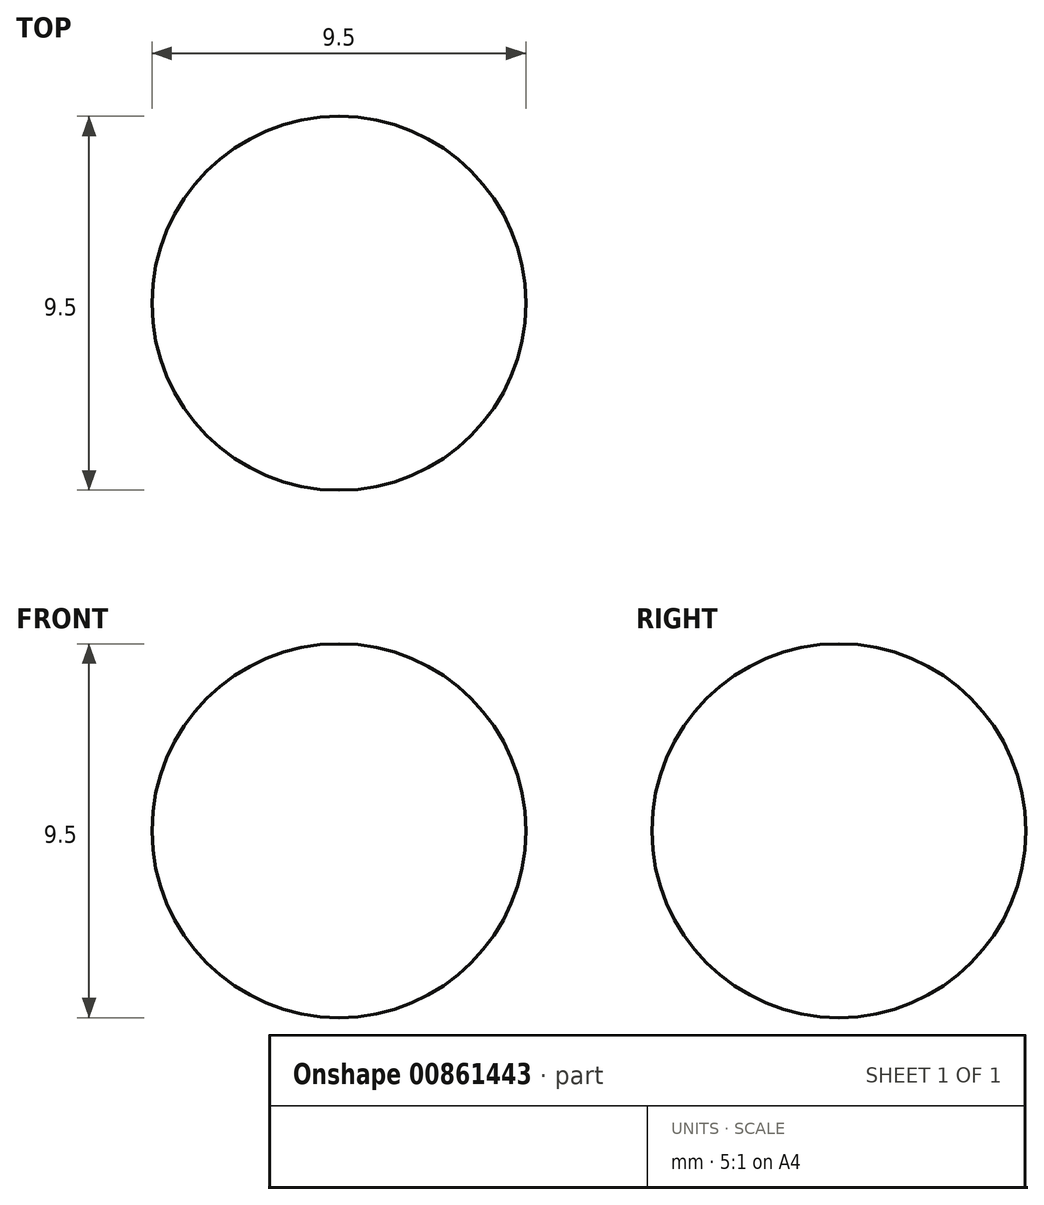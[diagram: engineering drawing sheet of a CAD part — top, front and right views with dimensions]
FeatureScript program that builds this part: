
annotation { "Feature Type Name" : "Feature", "Feature Type Description" : "" }
export const myFeature = defineFeature(function(context is Context, id is Id, definition is map)
    precondition{}
    {
        {
            var Q0;
            Q0=qCreatedBy(makeId("Front.planeOp"),FACE);
            var sketch = newSketch(context, id + "F0", { "sketchPlane" : qUnion([Q0])});
            skCircle(sketch, "E0", {"center": v(0, 0) * mm, "radius": 4.75 * mm});
            skLineSegment(sketch, "E1", {"start": v(0, 4.75) * mm, "end": v(0, -4.75) * mm});
            skSolve(sketch);
        }
        {
            var Q0;
            {var subQ0=sQuery(id+"F0.wireOp",EDGE,"E1");Q0=makeQuery(id+"F0.imprint","IMPRINT",FACE,{"disambiguationData":[TD([[makeQuery(id+"F0.imprint","IMPRINT",EDGE,{"derivedFrom":subQ0}),1.0]])]});}
            var Q1;
            Q1=sQuery(id+"F0.wireOp",EDGE,"E1");
            revolve(context, id + "F1", {"surfaceOperationType" : NewSurfaceOperationType.NEW, "entities" : qUnion([Q0]), "axis" : qUnion([Q1]), "revolveType" : RevolveType.FULL});
        }
    });
